# Revit family: Haworth_Immerse_StackTable_RectangleOnePieceTop
name_source: partatom
category: Furniture Systems
revit_build: Autodesk Revit 2018 (Build: 20170223_1515(x64)
units: mm (PartAtom-declared; Revit-internal decimal feet)

## family parameters
Always vertical = Yes
Cut with Voids When Loaded = No
OmniClass Number = 23.40.70.14.64.21
OmniClass Title = Systems Furniture
Part Type = Normal
Room Calculation Point = No
Round Connector Dimension = Use Diameter
Shared = No
Work Plane-Based = No

## types (4) — shared parameters
Actual Depth = 60"
Actual Height = 39"
Assembly Code = E2020200
Lower Top Cutout Depth = 12 1/2"
Lower Top Thickness = 1/8"
Manufacturer = Haworth
Revision Number = 1
Size = Verify Final Dim. w/ Haworth
Standard Height = 39 in.
Standard Sizes = 60d 96w, 60d 120w
URL = https://www.haworth.com
URL - Product = http://www.haworth.com
Understucture Thickness = 3 1/2"
Upper Top Thickness = 1 3/16"
Warranty = http://www.haworth.com

## per-type parameters (varying)
| type | 120 in. Width | 96 in. Width | Actual Width | Description | Lower Top Cutout Width | Lower Top Width | Model | Oblong Planter | Oblong Planter Void Height | Understructure Overall Width |
| 60d 120w 39h - No Planter | Yes | No | 120" | Haworth Immerse Stack Table Rectangle One Piece Top - 60d 120w 39h - No Planter | 78" | 118" | THRA-60C0 | No | 6" | 81" |
| 60d 120w 39h - Oblong Planter | Yes | No | 120" | Haworth Immerse Stack Table Rectangle One Piece Top - 60d 120w 39h - Oblong Planter | 78" | 118" | THRA-60C0 | Yes | 18" | 81" |
| 60d 96w 39h - No Planter | No | Yes | 96" | Haworth Immerse Stack Table Rectangle One Piece Top - 60d 96w 39h - No Planter | 54" | 94" | THRA-6096 | No | 6" | 57" |
| 60d 96w 39h - Oblong Planter | No | Yes | 96" | Haworth Immerse Stack Table Rectangle One Piece Top - 60d 96w 39h - Oblong Planter | 54" | 94" | THRA-6096 | Yes | 18" | 57" |

## geometry (parser evidence)
native form markers: Sweep x5
no freeform markers — native parametric forms only
